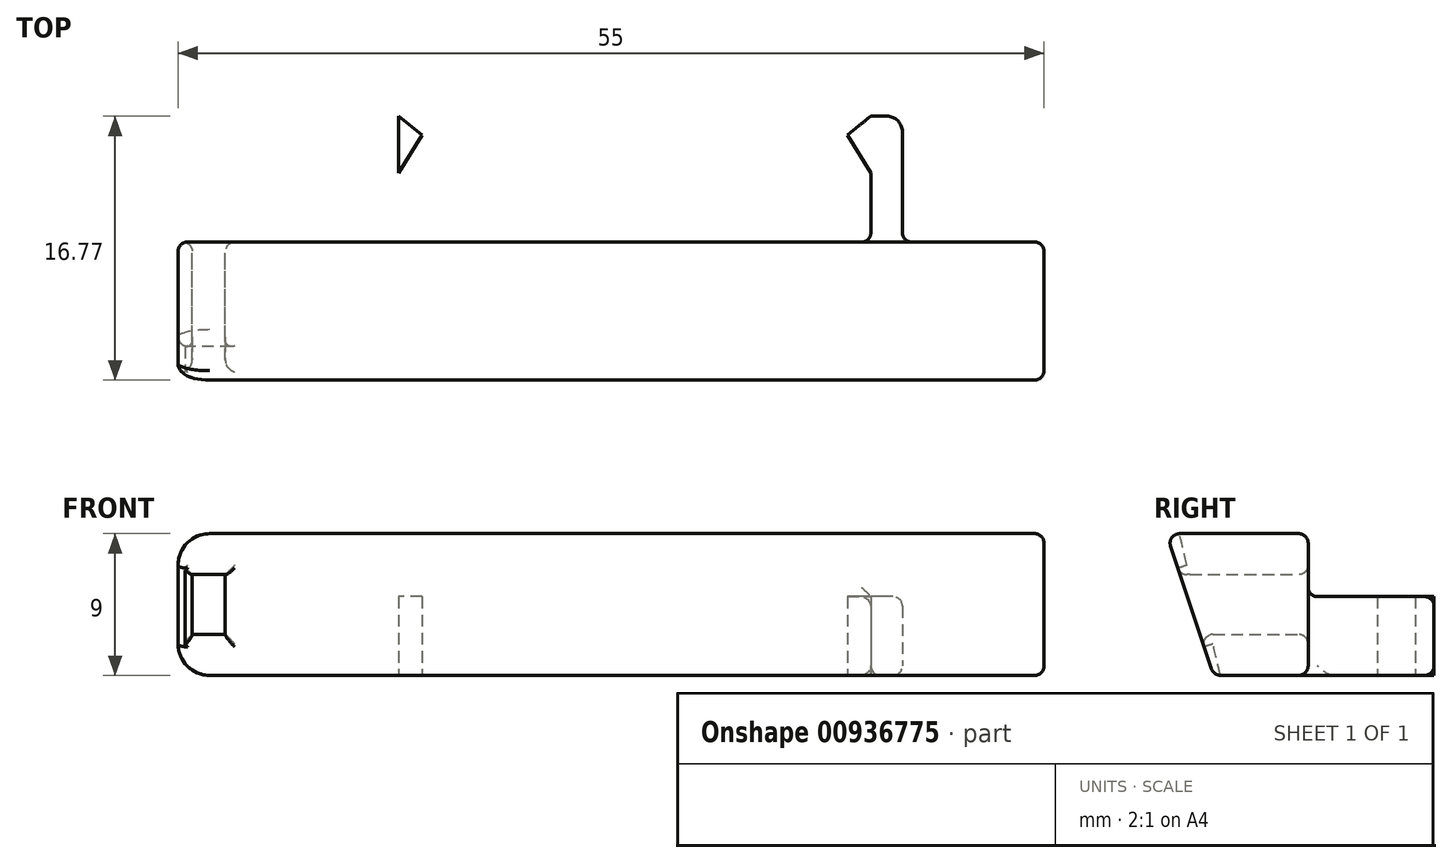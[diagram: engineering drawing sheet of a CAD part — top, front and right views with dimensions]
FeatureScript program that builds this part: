
annotation { "Feature Type Name" : "Feature", "Feature Type Description" : "" }
export const myFeature = defineFeature(function(context is Context, id is Id, definition is map)
    precondition{}
    {
        {
            var Q0;
            Q0=qCreatedBy(makeId("Top.planeOp"),FACE);
            var sketch = newSketch(context, id + "F0", { "sketchPlane" : qUnion([Q0])});
            skLineSegment(sketch, "E0", {"start": v(0, 0) * mm, "end": v(0, 25.9) * mm, "construction": true});
            skLineSegment(sketch, "E1.bottom", {"start": v(0, 0) * mm, "end": v(-26, 0) * mm});
            skLineSegment(sketch, "E1.top", {"start": v(0, 3) * mm, "end": v(-26, 3) * mm});
            skLineSegment(sketch, "E1.left", {"start": v(0, 0) * mm, "end": v(0, 3) * mm});
            skLineSegment(sketch, "E1.right", {"start": v(-26, 0) * mm, "end": v(-26, 3) * mm});
            skLineSegment(sketch, "E2.bottom", {"start": v(-17, 3) * mm, "end": v(-15, 3) * mm});
            skLineSegment(sketch, "E2.top", {"start": v(-16, 11) * mm, "end": v(-15, 11) * mm});
            skLineSegment(sketch, "E2.left", {"start": v(-17, 3) * mm, "end": v(-17, 10) * mm});
            skLineSegment(sketch, "E2.right", {"start": v(-15, 3) * mm, "end": v(-15, 11) * mm});
            skLineSegment(sketch, "E3", {"start": v(-15, 11) * mm, "end": v(-13.5, 9.8) * mm});
            skLineSegment(sketch, "E4", {"start": v(-13.5, 9.8) * mm, "end": v(-15, 7.4) * mm});
            skPoint(sketch, "E5.visualSharp", {"position": v(-17, 11) * mm});
            skArc(sketch, "E5.filletArc", {"start": v(-16, 11) * mm, "mid": v(-16.7, 10.7) * mm, "end": v(-17, 10) * mm});
            skLineSegment(sketch, "E6.MirrorCS", {"start": v(16, 11) * mm, "end": v(15, 11) * mm});
            skArc(sketch, "E7.MirrorCS", {"start": v(16, 11) * mm, "mid": v(16.7, 10.7) * mm, "end": v(17, 10) * mm});
            skLineSegment(sketch, "E8.MirrorCS", {"start": v(0, 0) * mm, "end": v(26, 0) * mm});
            skLineSegment(sketch, "E9.MirrorCS", {"start": v(17, 3) * mm, "end": v(15, 3) * mm});
            skLineSegment(sketch, "E10.MirrorCS", {"start": v(0, 3) * mm, "end": v(26, 3) * mm});
            skLineSegment(sketch, "E11.MirrorCS", {"start": v(17, 3) * mm, "end": v(17, 10) * mm});
            skLineSegment(sketch, "E12.MirrorCS", {"start": v(13.5, 9.8) * mm, "end": v(15, 7.4) * mm});
            skLineSegment(sketch, "E13.MirrorCS", {"start": v(26, 0) * mm, "end": v(26, 3) * mm});
            skLineSegment(sketch, "E14.MirrorCS", {"start": v(15, 3) * mm, "end": v(15, 11) * mm});
            skLineSegment(sketch, "E15.MirrorCS", {"start": v(15, 11) * mm, "end": v(13.5, 9.8) * mm});
            skPoint(sketch, "E16.MirrorP", {"position": v(17, 11) * mm});
            skLineSegment(sketch, "E17.bottom", {"start": v(-26, 0) * mm, "end": v(-29, 0) * mm});
            skLineSegment(sketch, "E17.top", {"start": v(-26, 3) * mm, "end": v(-29, 3) * mm});
            skLineSegment(sketch, "E17.right", {"start": v(-29, 0) * mm, "end": v(-29, 3) * mm});
            skSolve(sketch);
        }
        {
            var Q0;
            {var subQ1=sQuery(id+"F0.wireOp",EDGE,"E2.bottom");Q0=makeQuery(id+"F0.imprint","IMPRINT",FACE,{"disambiguationData":[TD([[makeQuery(id+"F0.imprint","IMPRINT",EDGE,{"derivedFrom":subQ1}),1.0]])]});}
            var Q1;
            {var subQ0=sQuery(id+"F0.wireOp",EDGE,"E3");Q1=makeQuery(id+"F0.imprint","IMPRINT",FACE,{"disambiguationData":[TD([[makeQuery(id+"F0.imprint","IMPRINT",EDGE,{"derivedFrom":subQ0}),-1.0]])]});}
            var Q2;
            {var subQ0=sQuery(id+"F0.wireOp",EDGE,"E12.MirrorCS");Q2=makeQuery(id+"F0.imprint","IMPRINT",FACE,{"disambiguationData":[TD([[makeQuery(id+"F0.imprint","IMPRINT",EDGE,{"derivedFrom":subQ0}),1.0]])]});}
            var Q3;
            {var subQ4=sQuery(id+"F0.wireOp",EDGE,"E6.MirrorCS");Q3=makeQuery(id+"F0.imprint","IMPRINT",FACE,{"disambiguationData":[TD([[makeQuery(id+"F0.imprint","IMPRINT",EDGE,{"derivedFrom":subQ4}),1.0]])]});}
            extrude(context, id + "F1", {"entities" : qUnion([Q0, Q1, Q2, Q3]), "endBound" : BoundingType.SYMMETRIC, "depth" : 5 * mm, "offsetDistance" : 25 * mm});
        }
        {
            var Q0;
            Q0=makeQuery(id+"F0.imprint","IMPRINT",FACE,{"disambiguationData":[TD([[makeQuery(id+"F0.imprint","IMPRINT",EDGE,{"derivedFrom":sQuery(id+"F0.wireOp",EDGE,"E17.bottom")}),-1.0]])]});
            var Q1;
            Q1=makeQuery(id+"F0.imprint","IMPRINT",FACE,{"disambiguationData":[TD([[makeQuery(id+"F0.imprint","IMPRINT",EDGE,{"derivedFrom":sQuery(id+"F0.wireOp",EDGE,"E8.MirrorCS")}),1.0]])]});
            var Q2;
            Q2=makeQuery(id+"F0.imprint","IMPRINT",FACE,{"disambiguationData":[TD([[makeQuery(id+"F0.imprint","IMPRINT",EDGE,{"derivedFrom":sQuery(id+"F0.wireOp",EDGE,"E1.bottom")}),-1.0]])]});
            var Q3;
            Q3=makeQuery(id+"F1.opExtrude","CAP_FACE",FACE,{"disambiguationData":[OSD([sQuery(id+"F0.wireOp",EDGE,"E6.MirrorCS"),sQuery(id+"F0.wireOp",EDGE,"E7.MirrorCS"),sQuery(id+"F0.wireOp",EDGE,"E10.MirrorCS"),sQuery(id+"F0.wireOp",EDGE,"E11.MirrorCS"),sQuery(id+"F0.wireOp",EDGE,"E12.MirrorCS"),sQuery(id+"F0.wireOp",EDGE,"E14.MirrorCS"),sQuery(id+"F0.wireOp",EDGE,"E15.MirrorCS")])],"isStart":true});
            extrude(context, id + "F2", {"entities" : qUnion([Q0, Q1, Q2]), "operationType" : NewBodyOperationType.ADD, "endBound" : BoundingType.UP_TO_SURFACE, "oppositeDirection" : true, "depth" : 9 * mm, "endBoundEntityFace" : qUnion([Q3]), "offsetDistance" : 25 * mm, "hasSecondDirection" : true, "secondDirectionOppositeDirection" : false, "secondDirectionDepth" : (9 - 2.5) * mm});
        }
        {
            var Q0;
            Q0=makeQuery(id+"F2.opExtrude","SWEPT_FACE",FACE,{"disambiguationData":[OSD([sQuery(id+"F0.wireOp",EDGE,"E13.MirrorCS")])]});
            var sketch = newSketch(context, id + "F3", { "sketchPlane" : qUnion([Q0])});
            skLineSegment(sketch, "E18", {"start": v(0, 6.5) * mm, "end": v(-6, 6.5) * mm});
            skLineSegment(sketch, "E19", {"start": v(-6, 6.5) * mm, "end": v(-3, -2.5) * mm});
            skLineSegment(sketch, "E20", {"start": v(-3, -2.5) * mm, "end": v(0, -2.5) * mm});
            skSolve(sketch);
        }
        {
            var Q0;
            Q0=makeQuery(id+"F3.imprint","IMPRINT",FACE,{"disambiguationData":[TD([[makeQuery(id+"F3.imprint","IMPRINT",EDGE,{"derivedFrom":sQuery(id+"F3.wireOp",EDGE,"E18")}),1.0]])]});
            var Q1;
            Q1=makeQuery(id+"F2.opExtrude","SWEPT_FACE",FACE,{"disambiguationData":[OSD([sQuery(id+"F0.wireOp",EDGE,"E17.right")])]});
            extrude(context, id + "F4", {"entities" : qUnion([Q0]), "operationType" : NewBodyOperationType.ADD, "endBound" : BoundingType.UP_TO_SURFACE, "oppositeDirection" : true, "depth" : 25 * mm, "endBoundEntityFace" : qUnion([Q1]), "offsetDistance" : 25 * mm});
        }
        {
            var Q0;
            Q0=makeQuery(id+"F2.opExtrude","SWEPT_FACE",FACE,{"disambiguationData":[OSD([sQuery(id+"F0.wireOp",EDGE,"E1.top"),sQuery(id+"F0.wireOp",EDGE,"E2.bottom"),sQuery(id+"F0.wireOp",EDGE,"E10.MirrorCS"),sQuery(id+"F0.wireOp",EDGE,"E17.top")])]});
            var sketch = newSketch(context, id + "F5", { "sketchPlane" : qUnion([Q0])});
            skLineSegment(sketch, "E21", {"start": v(28.1, 2) * mm, "end": v(28.1, 3.9) * mm});
            skLineSegment(sketch, "E22", {"start": v(28.1, 3.9) * mm, "end": v(26, 3.9) * mm});
            skLineSegment(sketch, "E23", {"start": v(26, 3.9) * mm, "end": v(26, 0) * mm});
            skLineSegment(sketch, "E24.0", {"start": v(26.34, 2) * mm, "end": v(29, 2) * mm, "construction": true});
            skLineSegment(sketch, "E25.MirrorCS", {"start": v(28.1, 0.1) * mm, "end": v(26, 0.1) * mm});
            skLineSegment(sketch, "E26.MirrorCS", {"start": v(26, 0.1) * mm, "end": v(26, 3.9) * mm});
            skLineSegment(sketch, "E27.MirrorCS", {"start": v(28.1, 2) * mm, "end": v(28.1, 0.1) * mm});
            skPoint(sketch, "E28", {"position": v(29, 2) * mm});
            skSolve(sketch);
        }
        {
            var Q0;
            Q0=makeQuery(id+"F5.imprint","IMPRINT",FACE,{"disambiguationData":[TD([[makeQuery(id+"F5.imprint","IMPRINT",EDGE,{"derivedFrom":sQuery(id+"F5.wireOp",EDGE,"E21")}),1.0]])]});
            extrude(context, id + "F6", {"entities" : qUnion([Q0]), "operationType" : NewBodyOperationType.REMOVE, "endBound" : BoundingType.THROUGH_ALL, "oppositeDirection" : true, "depth" : 25 * mm, "offsetDistance" : 25 * mm});
        }
        {
            var Q0;
            Q0=makeQuery(id+"F2.opExtrude","CAP_EDGE",EDGE,{"disambiguationData":[OSD([sQuery(id+"F0.wireOp",EDGE,"E17.right")])],"isStart":false});
            var Q1;
            Q1=makeQuery(id+"F2.opExtrude","CAP_EDGE",EDGE,{"disambiguationData":[OSD([sQuery(id+"F0.wireOp",EDGE,"E17.right")])],"isStart":true});
            fillet(context, id + "F7", {"entities" : qUnion([Q0, Q1]), "radius" : 2 * mm, "tangentPropagation" : true, "allowEdgeOverflow" : false});
        }
        {
            var Q0;
            Q0=makeQuery(id+"F2.opExtrude","SWEPT_FACE",FACE,{"disambiguationData":[OSD([sQuery(id+"F0.wireOp",EDGE,"E1.bottom"),sQuery(id+"F0.wireOp",EDGE,"E8.MirrorCS"),sQuery(id+"F0.wireOp",EDGE,"E17.bottom")])]});
            var Q1;
            Q1=makeQuery(id+"F2.opExtrude","SWEPT_FACE",FACE,{"disambiguationData":[OSD([sQuery(id+"F0.wireOp",EDGE,"E1.top"),sQuery(id+"F0.wireOp",EDGE,"E2.bottom"),sQuery(id+"F0.wireOp",EDGE,"E10.MirrorCS"),sQuery(id+"F0.wireOp",EDGE,"E17.top")])]});
            var Q2;
            Q2=makeQuery(id+"F2.opExtrude","CAP_EDGE",EDGE,{"disambiguationData":[OSD([sQuery(id+"F0.wireOp",EDGE,"E13.MirrorCS")])],"isStart":false});
            var Q3;
            Q3=makeQuery(id+"F2.opExtrude","CAP_EDGE",EDGE,{"disambiguationData":[OSD([sQuery(id+"F0.wireOp",EDGE,"E13.MirrorCS")])],"isStart":true});
            var Q4;
            Q4=makeQuery(id+"F1.opExtrude","CAP_EDGE",EDGE,{"disambiguationData":[OSD([sQuery(id+"F0.wireOp",EDGE,"E2.left")])],"isStart":false});
            var Q5;
            Q5=makeQuery(id+"F1.opExtrude","CAP_EDGE",EDGE,{"disambiguationData":[OSD([sQuery(id+"F0.wireOp",EDGE,"E2.left")])],"isStart":true});
            var Q6;
            Q6=makeQuery(id+"F1.opExtrude","CAP_EDGE",EDGE,{"disambiguationData":[OSD([sQuery(id+"F0.wireOp",EDGE,"E11.MirrorCS")])],"isStart":true});
            var Q7;
            Q7=makeQuery(id+"F1.opExtrude","CAP_EDGE",EDGE,{"disambiguationData":[OSD([sQuery(id+"F0.wireOp",EDGE,"E11.MirrorCS")])],"isStart":false});
            var Q8;
            Q8=makeQuery(id+"F4.opExtrude","SWEPT_FACE",FACE,{"disambiguationData":[OSD([sQuery(id+"F3.wireOp",EDGE,"E19")])]});
            fillet(context, id + "F8", {"entities" : qUnion([Q0, Q1, Q2, Q3, Q4, Q5, Q6, Q7, Q8]), "radius" : .6 * mm, "tangentPropagation" : true, "allowEdgeOverflow" : false});
        }
    });
